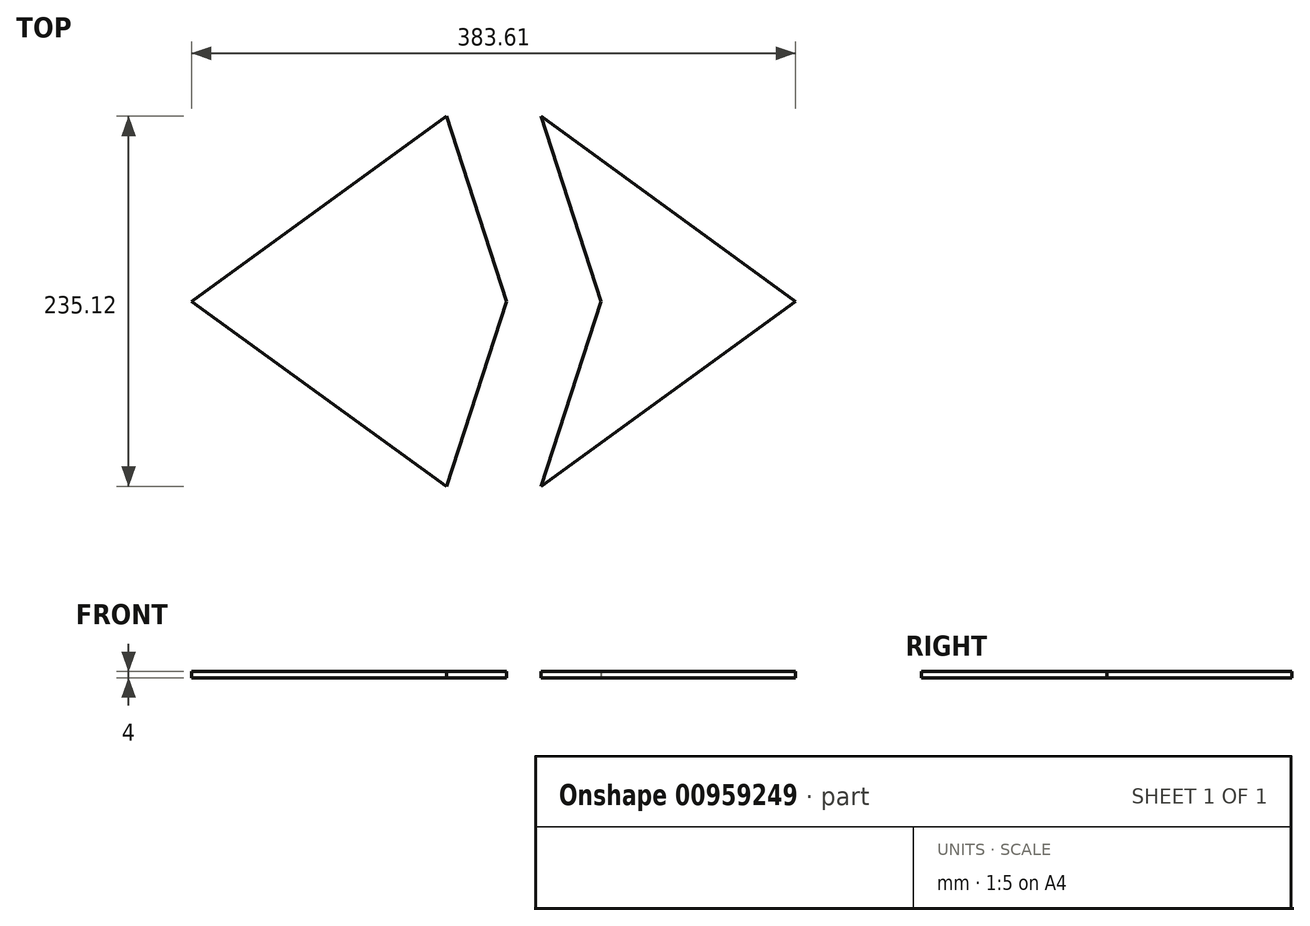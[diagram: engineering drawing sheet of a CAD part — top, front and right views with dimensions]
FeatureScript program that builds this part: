
annotation { "Feature Type Name" : "Feature", "Feature Type Description" : "" }
export const myFeature = defineFeature(function(context is Context, id is Id, definition is map)
    precondition{}
    {
        {
            var Q0;
            Q0=qCreatedBy(makeId("Top.planeOp"),FACE);
            var sketch = newSketch(context, id + "F0", { "sketchPlane" : qUnion([Q0])});
            skLineSegment(sketch, "E0", {"start": v(-230, 0) * mm, "end": v(-68.2, 117.56) * mm});
            skLineSegment(sketch, "E1", {"start": v(-68.2, 117.56) * mm, "end": v(-30, 0) * mm});
            skLineSegment(sketch, "E2", {"start": v(-30, 0) * mm, "end": v(-68.2, -117.56) * mm});
            skLineSegment(sketch, "E3", {"start": v(-68.2, -117.56) * mm, "end": v(-230, 0) * mm});
            skLineSegment(sketch, "E4", {"start": v(30, 0) * mm, "end": v(-8.2, 117.56) * mm});
            skLineSegment(sketch, "E5", {"start": v(-8.2, 117.56) * mm, "end": v(153.6, 0) * mm});
            skLineSegment(sketch, "E6", {"start": v(153.6, 0) * mm, "end": v(-8.2, -117.56) * mm});
            skLineSegment(sketch, "E7", {"start": v(-8.2, -117.56) * mm, "end": v(30, 0) * mm});
            skSolve(sketch);
        }
        {
            var Q0;
            Q0=makeQuery(id+"F0.imprint","IMPRINT",FACE,{"disambiguationData":[TD([[makeQuery(id+"F0.imprint","IMPRINT",EDGE,{"derivedFrom":sQuery(id+"F0.wireOp",EDGE,"E0")}),-1.0]])]});
            var Q1;
            Q1=makeQuery(id+"F0.imprint","IMPRINT",FACE,{"disambiguationData":[TD([[makeQuery(id+"F0.imprint","IMPRINT",EDGE,{"derivedFrom":sQuery(id+"F0.wireOp",EDGE,"E4")}),-1.0]])]});
            extrude(context, id + "F1", {"entities" : qUnion([Q0, Q1]), "depth" : 4 * mm, "offsetDistance" : 25 * mm});
        }
    });
